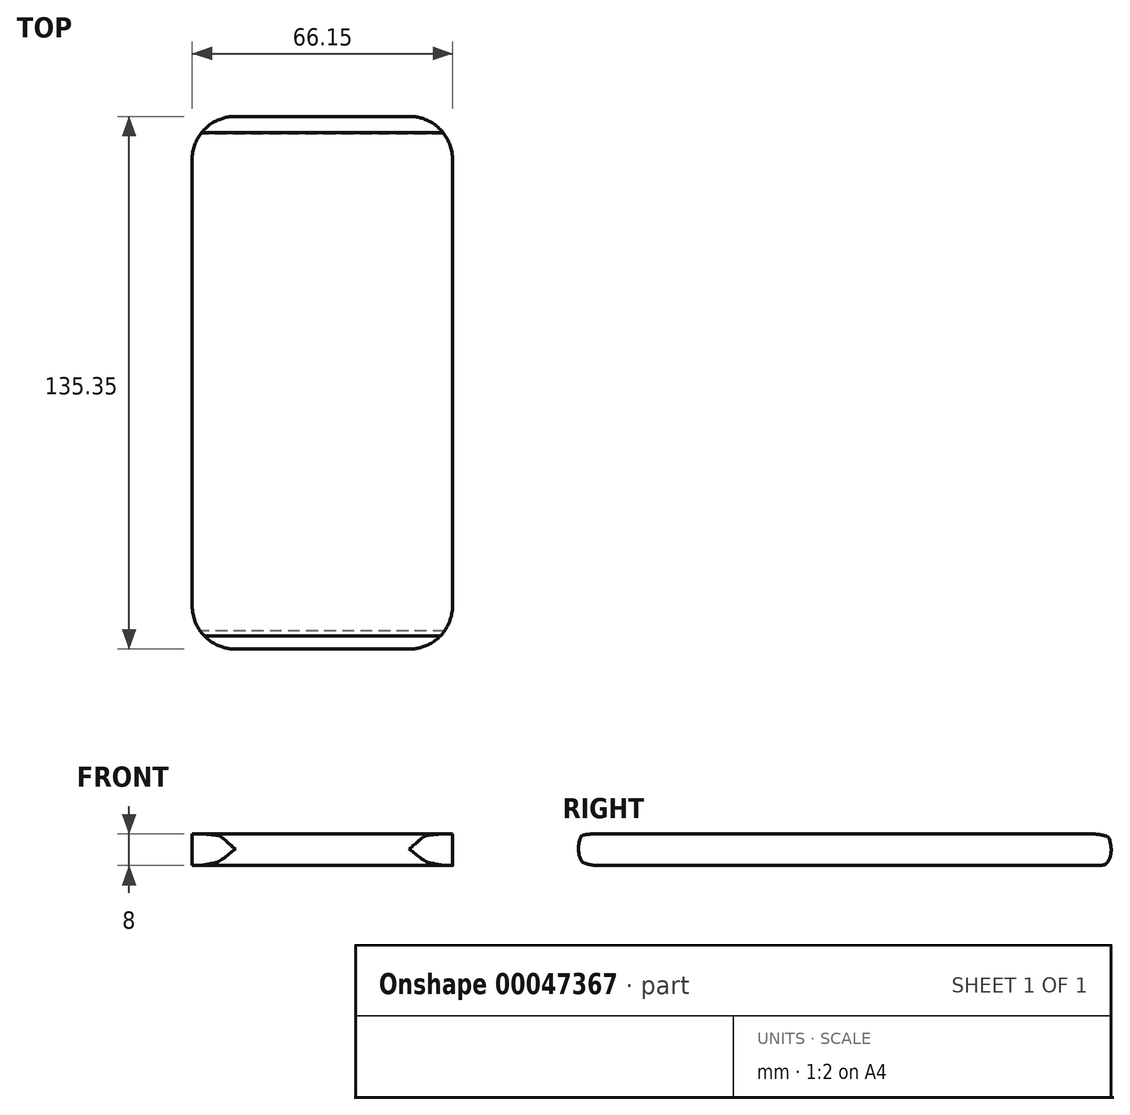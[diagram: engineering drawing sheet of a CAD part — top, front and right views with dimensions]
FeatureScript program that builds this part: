
annotation { "Feature Type Name" : "Feature", "Feature Type Description" : "" }
export const myFeature = defineFeature(function(context is Context, id is Id, definition is map)
    precondition{}
    {
        {
            var Q0;
            Q0=qCreatedBy(makeId("Top.planeOp"),FACE);
            var sketch = newSketch(context, id + "F0", { "sketchPlane" : qUnion([Q0])});
            skLineSegment(sketch, "E0.bottom", {"start": v(0, 0) * mm, "end": v(66.15, 0) * mm, "construction": true});
            skLineSegment(sketch, "E0.top", {"start": v(0, -135.35) * mm, "end": v(66.15, -135.35) * mm, "construction": true});
            skLineSegment(sketch, "E0.left", {"start": v(0, 0) * mm, "end": v(0, -135.35) * mm, "construction": true});
            skLineSegment(sketch, "E0.right", {"start": v(66.15, 0) * mm, "end": v(66.15, -135.35) * mm, "construction": true});
            skArc(sketch, "E1", {"start": v(11, 0) * mm, "mid": v(3.22, -3.22) * mm, "end": v(0, -11) * mm});
            skArc(sketch, "E2", {"start": v(66.15, -11) * mm, "mid": v(62.93, -3.22) * mm, "end": v(55.15, 0) * mm});
            skLineSegment(sketch, "E3", {"start": v(11, 0) * mm, "end": v(55.15, 0) * mm});
            skLineSegment(sketch, "E4", {"start": v(0, -11) * mm, "end": v(0, -124.35) * mm});
            skLineSegment(sketch, "E5", {"start": v(66.15, -11) * mm, "end": v(66.15, -124.35) * mm});
            skArc(sketch, "E6", {"start": v(0, -124.35) * mm, "mid": v(3.22, -132.13) * mm, "end": v(11, -135.35) * mm});
            skArc(sketch, "E7", {"start": v(55.15, -135.35) * mm, "mid": v(62.93, -132.13) * mm, "end": v(66.15, -124.35) * mm});
            skLineSegment(sketch, "E8", {"start": v(11, -135.35) * mm, "end": v(55.15, -135.35) * mm});
            skSolve(sketch);
        }
        {
            var Q0;
            Q0=qCreatedBy(makeId("Right.planeOp"),FACE);
            var sketch = newSketch(context, id + "F1", { "sketchPlane" : qUnion([Q0])});
            skLineSegment(sketch, "E9.bottom", {"start": v(0, 0) * mm, "end": v(-135.35, 0) * mm, "construction": true});
            skLineSegment(sketch, "E9.top", {"start": v(0, -8) * mm, "end": v(-135.35, -8) * mm, "construction": true});
            skLineSegment(sketch, "E9.left", {"start": v(0, 0) * mm, "end": v(0, -8) * mm, "construction": true});
            skLineSegment(sketch, "E9.right", {"start": v(-135.35, 0) * mm, "end": v(-135.35, -8) * mm, "construction": true});
            skPoint(sketch, "E10.10.internal.snap0", {"position": v(0, -4) * mm});
            skFitSpline(sketch, "E10", {"points": [v(-4.46, -8) * mm, v(-3.35, -7.96) * mm, v(-2.72, -7.93) * mm, v(-2.28, -7.9) * mm, v(-1.96, -7.84) * mm, v(-1.42, -7.6) * mm, v(-1.02, -7.24) * mm, v(-0.56, -6.53) * mm, v(-0.22, -5.55) * mm, v(-0.08, -4.88) * mm, v(0, -4) * mm, v(-0.14, -2.7) * mm, v(-0.3, -1.92) * mm, v(-0.47, -1.36) * mm, v(-0.63, -0.99) * mm, v(-0.78, -0.78) * mm, v(-1.08, -0.6) * mm, v(-1.66, -0.4) * mm, v(-2.3, -0.25) * mm, v(-2.97, -0.12) * mm, v(-3.72, -0.03) * mm, v(-4.12, 0) * mm], "startDerivative": vector(18.9, 0.52) * mm, "endDerivative": vector(-9.73, 0.8) * mm});
            skFitSpline(sketch, "E11", {"points": [v(-132, 0) * mm, v(-133.38, -0.11) * mm, v(-134.01, -0.24) * mm, v(-134.47, -0.4) * mm, v(-134.75, -0.73) * mm, v(-134.95, -1.22) * mm, v(-135.08, -1.68) * mm, v(-135.24, -2.5) * mm, v(-135.35, -3.83) * mm, v(-135.22, -5.17) * mm, v(-134.97, -6.05) * mm, v(-134.63, -6.73) * mm, v(-134.29, -7.15) * mm, v(-133.8, -7.4) * mm, v(-133, -7.65) * mm, v(-132.14, -7.85) * mm, v(-131.39, -7.93) * mm, v(-130.68, -8) * mm, v(-130.5, -8) * mm], "startDerivative": vector(-19.77, -1.13) * mm, "endDerivative": vector(5.52, 0.22) * mm});
            skLineSegment(sketch, "E12", {"start": v(-4.46, -8) * mm, "end": v(-130.5, -8) * mm});
            skLineSegment(sketch, "E13", {"start": v(-132, 0) * mm, "end": v(-4.12, 0) * mm});
            skLineSegment(sketch, "E14.bottom", {"start": v(2.5, 2.5) * mm, "end": v(-137.85, 2.5) * mm});
            skLineSegment(sketch, "E14.top", {"start": v(2.5, -10.5) * mm, "end": v(-137.85, -10.5) * mm});
            skLineSegment(sketch, "E14.left", {"start": v(2.5, 2.5) * mm, "end": v(2.5, -10.5) * mm});
            skLineSegment(sketch, "E14.right", {"start": v(-137.85, 2.5) * mm, "end": v(-137.85, -10.5) * mm});
            skSolve(sketch);
        }
        {
            var Q0;
            Q0 = qSketchRegion(id + "F0", true);
            extrude(context, id + "F2", {"entities" : qUnion([Q0]), "oppositeDirection" : true, "depth" : 8 * mm, "offsetDistance" : 25 * mm});
        }
        {
            var Q0;
            Q0=makeQuery(id+"F1.imprint","IMPRINT",FACE,{"disambiguationData":[TD([[makeQuery(id+"F1.imprint","IMPRINT",EDGE,{"derivedFrom":sQuery(id+"F1.wireOp",EDGE,"E10")}),-1.0]])]});
            extrude(context, id + "F3", {"entities" : qUnion([Q0]), "operationType" : NewBodyOperationType.REMOVE, "endBound" : BoundingType.THROUGH_ALL, "depth" : 25 * mm, "offsetDistance" : 25 * mm});
        }
    });
